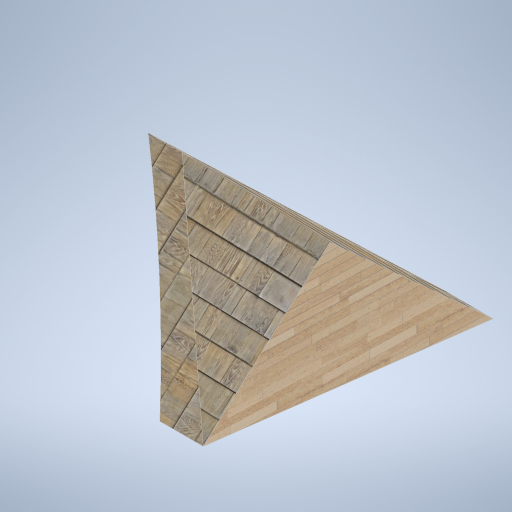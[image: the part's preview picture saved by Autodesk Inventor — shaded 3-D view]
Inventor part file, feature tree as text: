
AUTODESK INVENTOR PART (.ipt)
format: ipt  version: 2024.2 (Build 282272000, 272)  size: 449,536 bytes
history: native  units: in
note: dims shown in document units (in); Inventor stores cm internally (conversion verified against a paired STEP export)
features: sketch x7, plane x6, other x3
ambient origin geometry x8: Origin, YZ Plane, XZ Plane, XY Plane, X Axis, Y Axis, Z Axis, Center Point
bodies: Solid1 (feature_tree)
feature tree (16):
  other  "panel_pad_02 .ipt"
  other  "Solid1::panel_pad_02 .ipt"
  other  "TaggingFeature1"
  sketch  "Sketch1"  dims[d0=0.3937in]
  sketch  "Sketch2"
  sketch  "Sketch3"
  sketch  "Sketch6"
  sketch  "Sketch7"
  sketch  "Sketch8"
  sketch  "Sketch9"
  plane  "Work Plane1"
  plane  "Work Plane2"
  plane  "Work Plane3"
  plane  "Work Plane4"
  plane  "Work Plane5"
  plane  "Work Plane6"
